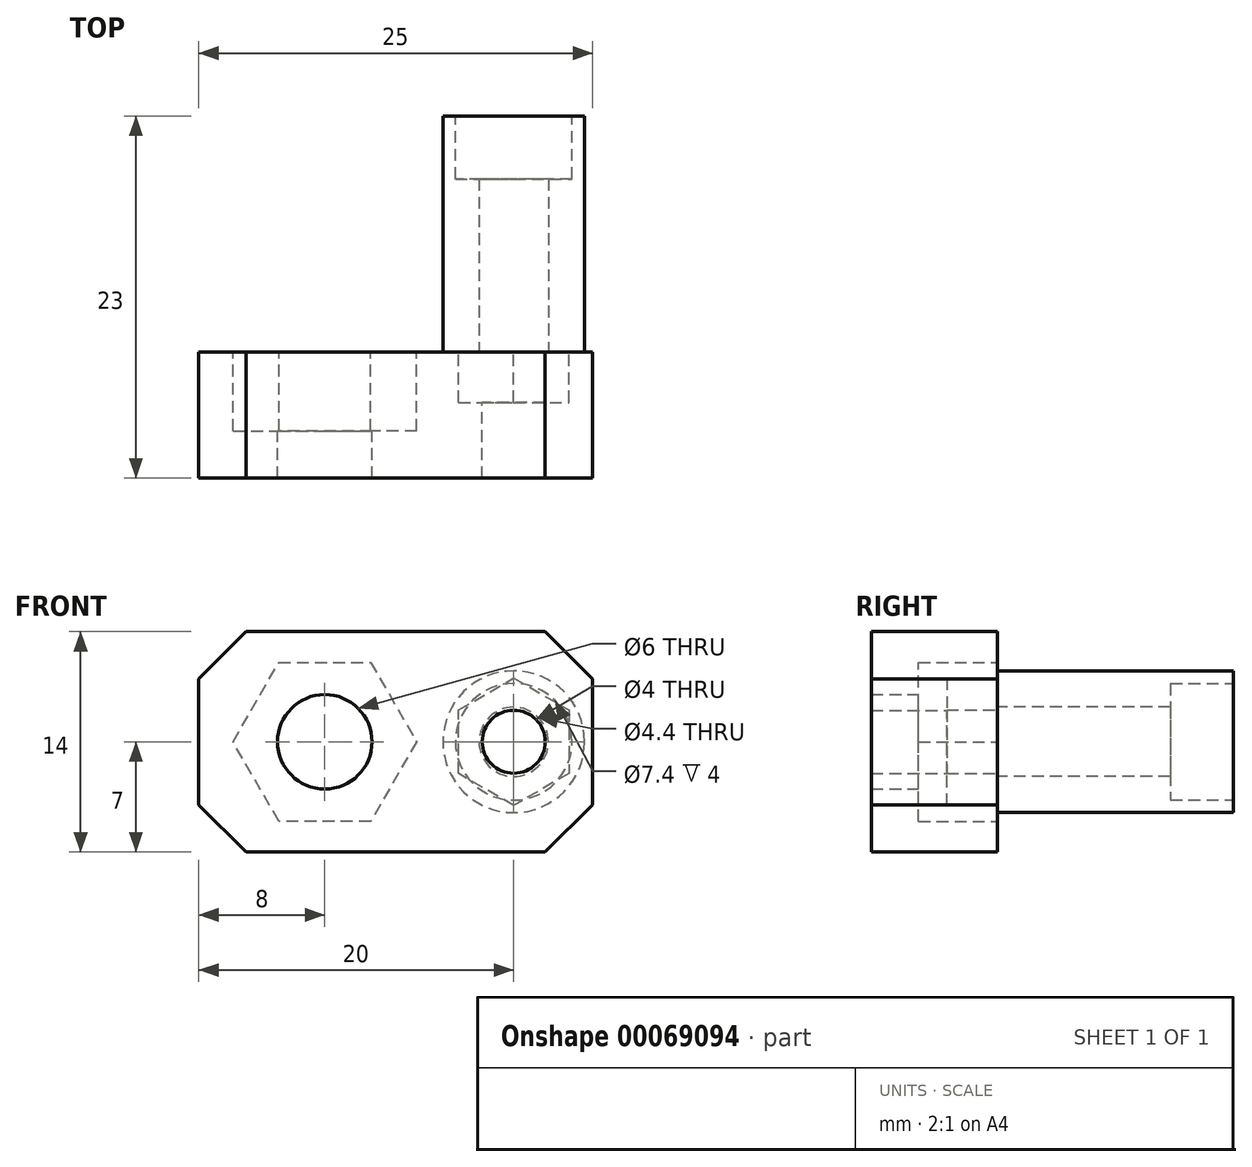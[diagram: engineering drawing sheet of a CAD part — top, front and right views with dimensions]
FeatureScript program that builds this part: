
annotation { "Feature Type Name" : "Feature", "Feature Type Description" : "" }
export const myFeature = defineFeature(function(context is Context, id is Id, definition is map)
    precondition{}
    {
        {
            var Q0;
            Q0=qCreatedBy(makeId("Front.planeOp"),FACE);
            var sketch = newSketch(context, id + "F0", { "sketchPlane" : qUnion([Q0])});
            skCircle(sketch, "E0.cCircle", {"center": v(0, 0) * mm, "radius": 5.05 * mm, "construction": true});
            skLineSegment(sketch, "E0.0", {"start": v(-2.92, 5.05) * mm, "end": v(2.92, 5.05) * mm});
            skLineSegment(sketch, "E0.1", {"start": v(2.92, 5.05) * mm, "end": v(5.83, 0) * mm});
            skLineSegment(sketch, "E0.2", {"start": v(5.83, 0) * mm, "end": v(2.92, -5.05) * mm});
            skLineSegment(sketch, "E0.3", {"start": v(2.92, -5.05) * mm, "end": v(-2.92, -5.05) * mm});
            skLineSegment(sketch, "E0.4", {"start": v(-2.92, -5.05) * mm, "end": v(-5.83, 0) * mm});
            skLineSegment(sketch, "E0.5", {"start": v(-5.83, 0) * mm, "end": v(-2.92, 5.05) * mm});
            skPoint(sketch, "E0.0.midPoint", {"position": v(0, 5.05) * mm});
            skLineSegment(sketch, "E1.bottom", {"start": v(-8, 7) * mm, "end": v(17, 7) * mm});
            skLineSegment(sketch, "E1.top", {"start": v(-8, -7) * mm, "end": v(17, -7) * mm});
            skLineSegment(sketch, "E1.left", {"start": v(-8, 7) * mm, "end": v(-8, -7) * mm});
            skLineSegment(sketch, "E1.right", {"start": v(17, 7) * mm, "end": v(17, -7) * mm});
            skPoint(sketch, "E1.middle", {"position": v(4.5, 0) * mm});
            skCircle(sketch, "E2.cCircle", {"center": v(12, 0) * mm, "radius": 3.5 * mm, "construction": true});
            skLineSegment(sketch, "E2.0", {"start": v(15.5, 2.02) * mm, "end": v(15.5, -2.02) * mm});
            skLineSegment(sketch, "E2.1", {"start": v(15.5, -2.02) * mm, "end": v(12, -4.04) * mm});
            skLineSegment(sketch, "E2.2", {"start": v(12, -4.04) * mm, "end": v(8.5, -2.02) * mm});
            skLineSegment(sketch, "E2.3", {"start": v(8.5, -2.02) * mm, "end": v(8.5, 2.02) * mm});
            skLineSegment(sketch, "E2.4", {"start": v(8.5, 2.02) * mm, "end": v(12, 4.04) * mm});
            skLineSegment(sketch, "E2.5", {"start": v(12, 4.04) * mm, "end": v(15.5, 2.02) * mm});
            skPoint(sketch, "E2.0.midPoint", {"position": v(15.5, 0) * mm});
            skCircle(sketch, "E3", {"center": v(0, 0) * mm, "radius": 3 * mm});
            skCircle(sketch, "E4", {"center": v(12, 0) * mm, "radius": 2 * mm});
            skSolve(sketch);
        }
        {
            var Q0;
            Q0=makeQuery(id+"F0.imprint","IMPRINT",FACE,{"disambiguationData":[TD([[makeQuery(id+"F0.imprint","IMPRINT",EDGE,{"derivedFrom":sQuery(id+"F0.wireOp",EDGE,"E0.0")}),-1.0]])]});
            var Q1;
            Q1=makeQuery(id+"F0.imprint","IMPRINT",FACE,{"disambiguationData":[TD([[makeQuery(id+"F0.imprint","IMPRINT",EDGE,{"derivedFrom":sQuery(id+"F0.wireOp",EDGE,"E0.0")}),1.0]])]});
            var Q2;
            Q2=makeQuery(id+"F0.imprint","IMPRINT",FACE,{"disambiguationData":[TD([[makeQuery(id+"F0.imprint","IMPRINT",EDGE,{"derivedFrom":sQuery(id+"F0.wireOp",EDGE,"E2.0")}),-1.0]])]});
            extrude(context, id + "F1", {"entities" : qUnion([Q0, Q1, Q2]), "depth" : 8 * mm, "offsetDistance" : 25 * mm});
        }
        {
            var Q0;
            Q0=makeQuery(id+"F0.imprint","IMPRINT",FACE,{"disambiguationData":[TD([[makeQuery(id+"F0.imprint","IMPRINT",EDGE,{"derivedFrom":sQuery(id+"F0.wireOp",EDGE,"E0.0")}),-1.0]])]});
            extrude(context, id + "F2", {"entities" : qUnion([Q0]), "operationType" : NewBodyOperationType.REMOVE, "depth" : 5 * mm, "offsetDistance" : 25 * mm});
        }
        {
            var Q0;
            Q0=makeQuery(id+"F0.imprint","IMPRINT",FACE,{"disambiguationData":[TD([[makeQuery(id+"F0.imprint","IMPRINT",EDGE,{"derivedFrom":sQuery(id+"F0.wireOp",EDGE,"E2.0")}),-1.0]])]});
            extrude(context, id + "F3", {"entities" : qUnion([Q0]), "operationType" : NewBodyOperationType.REMOVE, "depth" : 3.2 * mm, "offsetDistance" : 25 * mm});
        }
        {
            var Q0;
            Q0=makeQuery(id+"F1.opExtrude","SWEPT_EDGE",EDGE,{"disambiguationData":[OSD([sQuery(id+"F0.wireOp",EDGE,"E1.top"),sQuery(id+"F0.wireOp",EDGE,"E1.left")])]});
            var Q1;
            Q1=makeQuery(id+"F1.opExtrude","SWEPT_EDGE",EDGE,{"disambiguationData":[OSD([sQuery(id+"F0.wireOp",EDGE,"E1.top"),sQuery(id+"F0.wireOp",EDGE,"E1.right")])]});
            var Q2;
            Q2=makeQuery(id+"F1.opExtrude","SWEPT_EDGE",EDGE,{"disambiguationData":[OSD([sQuery(id+"F0.wireOp",EDGE,"E1.bottom"),sQuery(id+"F0.wireOp",EDGE,"E1.left")])]});
            var Q3;
            Q3=makeQuery(id+"F1.opExtrude","SWEPT_EDGE",EDGE,{"disambiguationData":[OSD([sQuery(id+"F0.wireOp",EDGE,"E1.bottom"),sQuery(id+"F0.wireOp",EDGE,"E1.right")])]});
            chamfer(context, id + "F4", {"entities" : qUnion([Q0, Q1, Q2, Q3]), "width" : 3 * mm, "tangentPropagation" : true});
        }
        {
            var Q0;
            Q0=makeQuery(id+"F1.opExtrude","CAP_FACE",FACE,{"disambiguationData":[OSD([sQuery(id+"F0.wireOp",EDGE,"E1.bottom"),sQuery(id+"F0.wireOp",EDGE,"E1.top"),sQuery(id+"F0.wireOp",EDGE,"E1.left"),sQuery(id+"F0.wireOp",EDGE,"E1.right"),sQuery(id+"F0.wireOp",EDGE,"E3"),sQuery(id+"F0.wireOp",EDGE,"E4")])],"isStart":true});
            var sketch = newSketch(context, id + "F5", { "sketchPlane" : qUnion([Q0])});
            skCircle(sketch, "E5", {"center": v(-12, 0) * mm, "radius": 4.5 * mm});
            skCircle(sketch, "E6", {"center": v(-12, 0) * mm, "radius": 2.2 * mm});
            skSolve(sketch);
        }
        {
            var Q0;
            Q0 = qSketchRegion(id + "F5", true);
            extrude(context, id + "F6", {"entities" : qUnion([Q0]), "depth" : 15 * mm, "offsetDistance" : 25 * mm});
        }
        {
            var Q0;
            Q0=makeQuery(id+"F6.opExtrude","CAP_FACE",FACE,{"disambiguationData":[OSD([sQuery(id+"F5.wireOp",EDGE,"E5"),sQuery(id+"F5.wireOp",EDGE,"E6")])],"isStart":false});
            var sketch = newSketch(context, id + "F7", { "sketchPlane" : qUnion([Q0])});
            skCircle(sketch, "E7", {"center": v(-12, 0) * mm, "radius": 3.7 * mm});
            skSolve(sketch);
        }
        {
            var Q0;
            Q0 = qSketchRegion(id + "F7", true);
            extrude(context, id + "F8", {"entities" : qUnion([Q0]), "operationType" : NewBodyOperationType.REMOVE, "oppositeDirection" : true, "depth" : 4 * mm, "offsetDistance" : 25 * mm});
        }
    });
